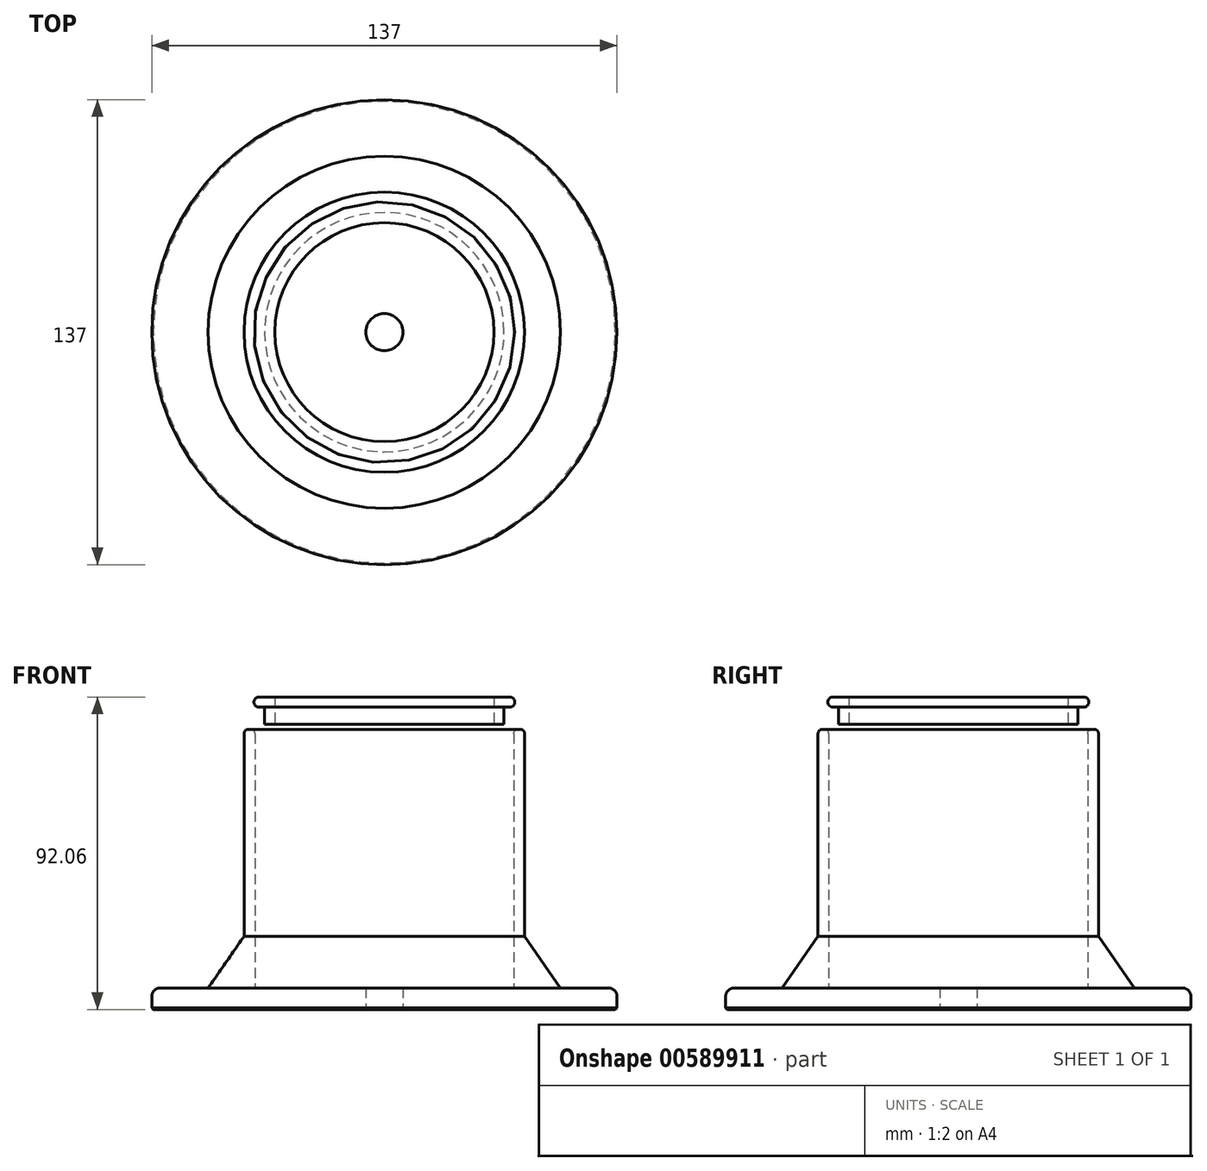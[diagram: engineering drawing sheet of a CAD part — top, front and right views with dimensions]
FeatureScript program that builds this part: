
annotation { "Feature Type Name" : "Feature", "Feature Type Description" : "" }
export const myFeature = defineFeature(function(context is Context, id is Id, definition is map)
    precondition{}
    {
        {
            assignVariable(context, id + "F0", {"name" : "baseheight", "anyValue" : 6.35 * mm});
        }
        {
            assignVariable(context, id + "F1", {"name" : "wallthick", "anyValue" : 3.17 * mm});
        }
        {
            var Q0;
            Q0=qCreatedBy(makeId("Front.planeOp"),FACE);
            var sketch = newSketch(context, id + "F2", { "sketchPlane" : qUnion([Q0])});
            skLineSegment(sketch, "E0", {"start": v(-68.5, 6.35) * mm, "end": v(-68.5, 0) * mm});
            skLineSegment(sketch, "E1", {"start": v(-68.5, 0) * mm, "end": v(0, 0) * mm});
            skLineSegment(sketch, "E2", {"start": v(0, 0) * mm, "end": v(0, 6.35) * mm});
            skLineSegment(sketch, "E3", {"start": v(0, 6.35) * mm, "end": v(-38.12, 6.35) * mm});
            skLineSegment(sketch, "E4", {"start": v(-38.12, 6.35) * mm, "end": v(-38.12, 82.55) * mm});
            skLineSegment(sketch, "E5", {"start": v(-38.12, 82.55) * mm, "end": v(-41.3, 82.55) * mm});
            skLineSegment(sketch, "E6", {"start": v(-41.3, 82.55) * mm, "end": v(-41.3, 21.59) * mm});
            skLineSegment(sketch, "E7", {"start": v(-41.3, 21.59) * mm, "end": v(-51.88, 6.35) * mm});
            skLineSegment(sketch, "E8", {"start": v(-51.88, 6.35) * mm, "end": v(-68.5, 6.35) * mm});
            skSolve(sketch);
        }
        {
            var Q0;
            Q0=qCreatedBy(makeId("Front.planeOp"),FACE);
            var sketch = newSketch(context, id + "F3", { "sketchPlane" : qUnion([Q0])});
            skLineSegment(sketch, "E9", {"start": v(0, 0) * mm, "end": v(0, 82.2) * mm, "construction": true});
            skSolve(sketch);
        }
        {
            var Q0;
            Q0=qCreatedBy(makeId("Front.planeOp"),FACE);
            var sketch = newSketch(context, id + "F4", { "sketchPlane" : qUnion([Q0])});
            skLineSegment(sketch, "E10", {"start": v(-35.25, 84.06) * mm, "end": v(-35.25, 89.06) * mm});
            skLineSegment(sketch, "E11", {"start": v(-35.25, 89.06) * mm, "end": v(-38.43, 89.06) * mm});
            skLineSegment(sketch, "E12", {"start": v(-38.43, 89.06) * mm, "end": v(-38.43, 92.06) * mm});
            skLineSegment(sketch, "E13", {"start": v(-38.43, 92.06) * mm, "end": v(-32.25, 92.06) * mm});
            skLineSegment(sketch, "E14", {"start": v(-32.25, 92.06) * mm, "end": v(-32.25, 84.06) * mm});
            skLineSegment(sketch, "E15", {"start": v(-32.25, 84.06) * mm, "end": v(-35.25, 84.06) * mm});
            skLineSegment(sketch, "E16", {"start": v(0, 68.8) * mm, "end": v(0, 95.4) * mm, "construction": true});
            skLineSegment(sketch, "E17", {"start": v(0, 85.18) * mm, "end": v(-32.25, 85.18) * mm, "construction": true});
            skSolve(sketch);
        }
        {
            var Q0;
            Q0=makeQuery(id+"F2.imprint","IMPRINT",FACE,{"disambiguationData":[TD([[makeQuery(id+"F2.imprint","IMPRINT",EDGE,{"derivedFrom":sQuery(id+"F2.wireOp",EDGE,"E0")}),1.0]])]});
            var Q1;
            Q1=sQuery(id+"F2.wireOp",EDGE,"E2");
            revolve(context, id + "F5", {"entities" : qUnion([Q0]), "axis" : qUnion([Q1]), "revolveType" : RevolveType.FULL});
        }
        {
            var Q0;
            Q0=makeQuery(id+"F5.opRevolve","SWEPT_EDGE",EDGE,{"disambiguationData":[OSD([sQuery(id+"F2.wireOp",EDGE,"E0"),sQuery(id+"F2.wireOp",EDGE,"E8")])]});
            fillet(context, id + "F6", {"entities" : qUnion([Q0]), "radius" : getVariable(context, 'baseheight') * 0.4, "tangentPropagation" : true, "allowEdgeOverflow" : false});
        }
        {
            var Q0;
            Q0=qCreatedBy(makeId("Top.planeOp"),FACE);
            var sketch = newSketch(context, id + "F7", { "sketchPlane" : qUnion([Q0])});
            skCircle(sketch, "E18", {"center": v(0, 0) * mm, "radius": 5.46 * mm});
            skSolve(sketch);
        }
        {
            var Q0;
            Q0=qSketchRegion(id+"F7",true);
            extrude(context, id + "F8", {"entities" : qUnion([Q0]), "operationType" : NewBodyOperationType.REMOVE, "endBound" : BoundingType.THROUGH_ALL, "depth" : getVariable(context, 'baseheight'), "offsetDistance" : 25 * mm});
        }
        {
            var Q0;
            Q0=makeQuery(id+"F5.opRevolve","SWEPT_EDGE",EDGE,{"disambiguationData":[OSD([sQuery(id+"F2.wireOp",EDGE,"E0"),sQuery(id+"F2.wireOp",EDGE,"E1")])]});
            chamfer(context, id + "F9", {"entities" : qUnion([Q0]), "width" : 0.5 * mm, "tangentPropagation" : true});
        }
        {
            var Q0;
            Q0=makeQuery(id+"F5.opRevolve","SWEPT_EDGE",EDGE,{"disambiguationData":[OSD([sQuery(id+"F2.wireOp",EDGE,"E4"),sQuery(id+"F2.wireOp",EDGE,"E5")])]});
            fillet(context, id + "F10", {"entities" : qUnion([Q0]), "radius" : getVariable(context, 'wallthick') * 0.4, "tangentPropagation" : true, "allowEdgeOverflow" : false});
        }
        {
            var Q0;
            Q0=makeQuery(id+"F5.opRevolve","SWEPT_EDGE",EDGE,{"disambiguationData":[OSD([sQuery(id+"F2.wireOp",EDGE,"E5"),sQuery(id+"F2.wireOp",EDGE,"E6")])]});
            fillet(context, id + "F11", {"entities" : qUnion([Q0]), "radius" : getVariable(context, 'wallthick') * 0.4, "tangentPropagation" : true, "allowEdgeOverflow" : false});
        }
        {
            var Q0;
            Q0=qSketchRegion(id+"F4",true);
            var Q1;
            Q1=sQuery(id+"F3.wireOp",EDGE,"E9");
            revolve(context, id + "F12", {"entities" : qUnion([Q0]), "axis" : qUnion([Q1]), "revolveType" : RevolveType.FULL});
        }
        {
            var Q0;
            Q0=makeQuery(id+"F12.opRevolve","SWEPT_EDGE",EDGE,{"disambiguationData":[OSD([sQuery(id+"F4.wireOp",EDGE,"E12"),sQuery(id+"F4.wireOp",EDGE,"E13")])]});
            fillet(context, id + "F13", {"entities" : qUnion([Q0]), "radius" : 1.5 * mm, "tangentPropagation" : true, "allowEdgeOverflow" : false});
        }
        {
            var Q0;
            Q0=makeQuery(id+"F12.opRevolve","SWEPT_EDGE",EDGE,{"disambiguationData":[OSD([sQuery(id+"F4.wireOp",EDGE,"E11"),sQuery(id+"F4.wireOp",EDGE,"E12")])]});
            var Q1;
            Q1=makeQuery(id+"F12.opRevolve","SWEPT_FACE",FACE,{"disambiguationData":[OSD([sQuery(id+"F4.wireOp",EDGE,"E12")])]});
            fillet(context, id + "F14", {"entities" : qUnion([Q0, Q1]), "radius" : 1.5 * mm, "tangentPropagation" : true, "allowEdgeOverflow" : false});
        }
    });
